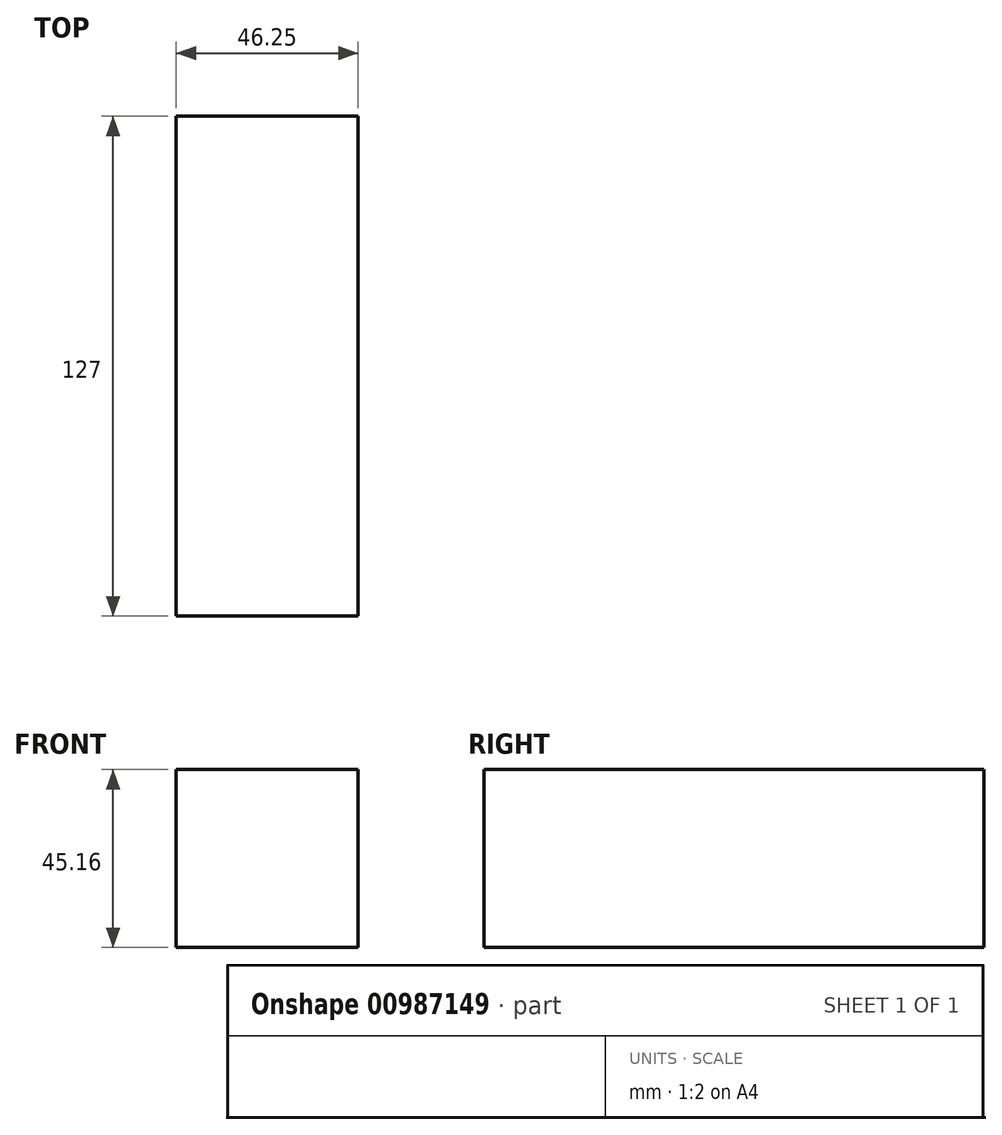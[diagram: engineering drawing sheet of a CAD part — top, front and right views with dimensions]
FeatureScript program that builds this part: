
annotation { "Feature Type Name" : "Feature", "Feature Type Description" : "" }
export const myFeature = defineFeature(function(context is Context, id is Id, definition is map)
    precondition{}
    {
        {
            var Q0;
            Q0=qCreatedBy(makeId("Front.planeOp"),FACE);
            var sketch = newSketch(context, id + "F0", { "sketchPlane" : qUnion([Q0])});
            skLineSegment(sketch, "E0.bottom", {"start": v(0, 0) * mm, "end": v(46.25, 0) * mm});
            skLineSegment(sketch, "E0.top", {"start": v(0, 45.16) * mm, "end": v(46.25, 45.16) * mm});
            skLineSegment(sketch, "E0.left", {"start": v(0, 0) * mm, "end": v(0, 45.16) * mm});
            skLineSegment(sketch, "E0.right", {"start": v(46.25, 0) * mm, "end": v(46.25, 45.16) * mm});
            skSolve(sketch);
        }
        {
            var Q0;
            Q0=makeQuery(id+"F0.imprint","IMPRINT",FACE,{"disambiguationData":[TD([[makeQuery(id+"F0.imprint","IMPRINT",EDGE,{"derivedFrom":sQuery(id+"F0.wireOp",EDGE,"E0.bottom")}),1.0]])]});
            extrude(context, id + "F1", {"entities" : qUnion([Q0]), "depth" : 127 * mm, "offsetDistance" : 25.4 * mm});
        }
    });
